# Revit family: LUXI_HIGH BAY LIGHT_PA
name_source: partatom
category: Apparecchi per illuminazione
revit_build: Autodesk Revit 2016 (Build: 20161004_0715(x64)
units: mm (PartAtom-declared; Revit-internal decimal feet)

## family parameters
Condiviso = No
Host = Superficie
Numero OmniClass = 23.80.70.00
Punto di calcolo locali = Sì
Quota connettore circolare = Usa diametro
Sorgente d'illuminazione = Sì
Taglio con vuoti quando caricato = No
Tipo di parte = Normale
Titolo OmniClass = Lighting

## types (2) — shared parameters
Alimentatore = Incluso
Alimentazione = 220-240V AC / 50-60 Hz
Angolo inclinazione = -90.00°
Articolo = HBPA150085W840D
Carico apparente = 120 VA
Certificazioni = CE / RohS
Classe di efficienza energetica = A+
Classe di protezione = I
Classe di rischio fotobiologico = Esente (RG0)
Colore = Bianco
Descrizione = Proiettore a Led
Diametro = 350 mm  [stored 1.14829 ft]
Dimensioni = Ø350x273
Emetti da diametro cerchio = 190 mm
Fattore di correzione di potenza = ≥0,95 (typ.)
File diagramma fotometrico = HBPA150085W840D Luxi SERIE PA 150W 4000K 120W.IES
Filtro dei colori = 16777215
Garanzia = 7 anni
Grado di protezione = IP 65 (frontale)
H = 273 mm  [stored 0.895669 ft]
IFCExportAs = IfcLightFixtureType
Indice di resa cromatica = ≥80 (typ.)
Masterformat 2016 Codice = 26.50.00
Masterformat 2016 Descrizione = Lighting
Materiale 1 = Alluminio_Bianco
Materiale 2 = Policarbonato Diffondente
Materiale 3 = Policarbonato Trasparente
Modello = Serie PA | High Bay Light
Ottiche = Fascio 85°
Peso = 6.70 kg
Potenza = 120 W
Produttore = Luxi Illuminazione S.r.l.
Prospetto di default = 2000 mm
Protezione agli urti = IK10 (20 Joule)
Regolazione del flusso luminoso = 1-10V
Rendi la forma visibile nel rendering = No
Revisione = 3
Sistema di illuminazione = 90% luce diretta / 10% luce indiretta
Sorgente = LED SMD
Step MacAdam (SDCM) = <4
Temperatura di esercizio = -40°C / +45°C
Tipologie di installazione = Sospensione
URL = https://www.luxi.lighting
Uniclass 2015 Codice = EF_70_80
Uniclass 2015 Descrizione = Lighting
Variazione temperatura colore lampada con luminosità attenuata = <Nessuno>
Vita utile = L70B20 50.000ore

## type names (no varying parameters)
- HBPA150085W840D
- HBPA150085W840D_120W

note: [stored X ft] marks values corroborated as IEEE doubles in the binary element streams (Revit-internal decimal feet)

## geometry (parser evidence)
native form markers: Blend x4
no freeform markers — native parametric forms only
